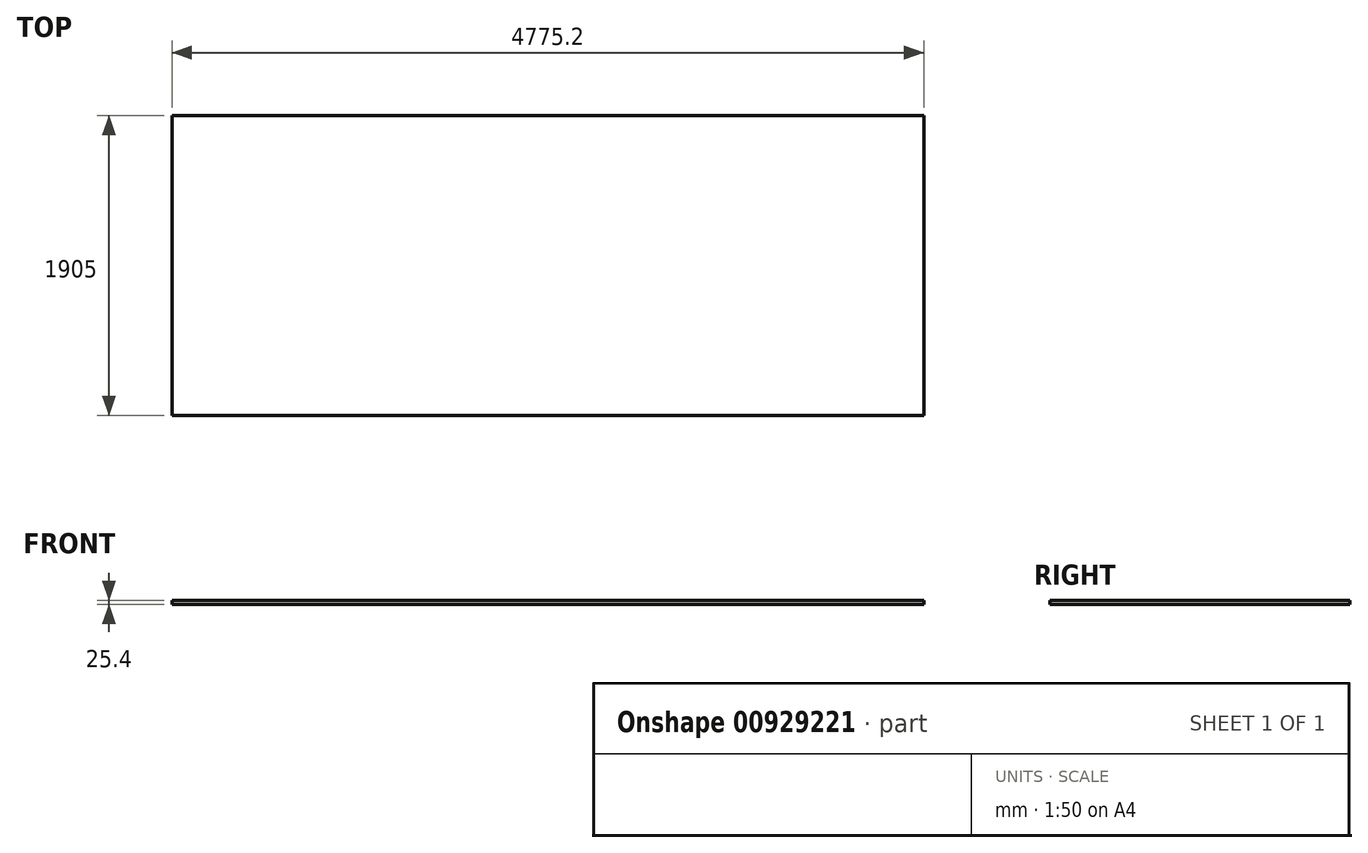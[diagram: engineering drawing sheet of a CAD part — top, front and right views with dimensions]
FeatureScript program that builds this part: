
annotation { "Feature Type Name" : "Feature", "Feature Type Description" : "" }
export const myFeature = defineFeature(function(context is Context, id is Id, definition is map)
    precondition{}
    {
        {
            var Q0;
            Q0=qCreatedBy(makeId("Top.planeOp"),FACE);
            var sketch = newSketch(context, id + "F0", { "sketchPlane" : qUnion([Q0])});
            skLineSegment(sketch, "E0.bottom", {"start": v(2387.6, 952.5) * mm, "end": v(-2387.6, 952.5) * mm});
            skLineSegment(sketch, "E0.top", {"start": v(2387.6, -952.5) * mm, "end": v(-2387.6, -952.5) * mm});
            skLineSegment(sketch, "E0.left", {"start": v(2387.6, 952.5) * mm, "end": v(2387.6, -952.5) * mm});
            skLineSegment(sketch, "E0.right", {"start": v(-2387.6, 952.5) * mm, "end": v(-2387.6, -952.5) * mm});
            skPoint(sketch, "E0.middle", {"position": v(0, 0) * mm});
            skSolve(sketch);
        }
        {
            var Q0;
            Q0 = qSketchRegion(id + "F0", true);
            extrude(context, id + "F1", {"entities" : qUnion([Q0]), "depth" : 25.4 * mm, "offsetDistance" : 25.4 * mm});
        }
    });
